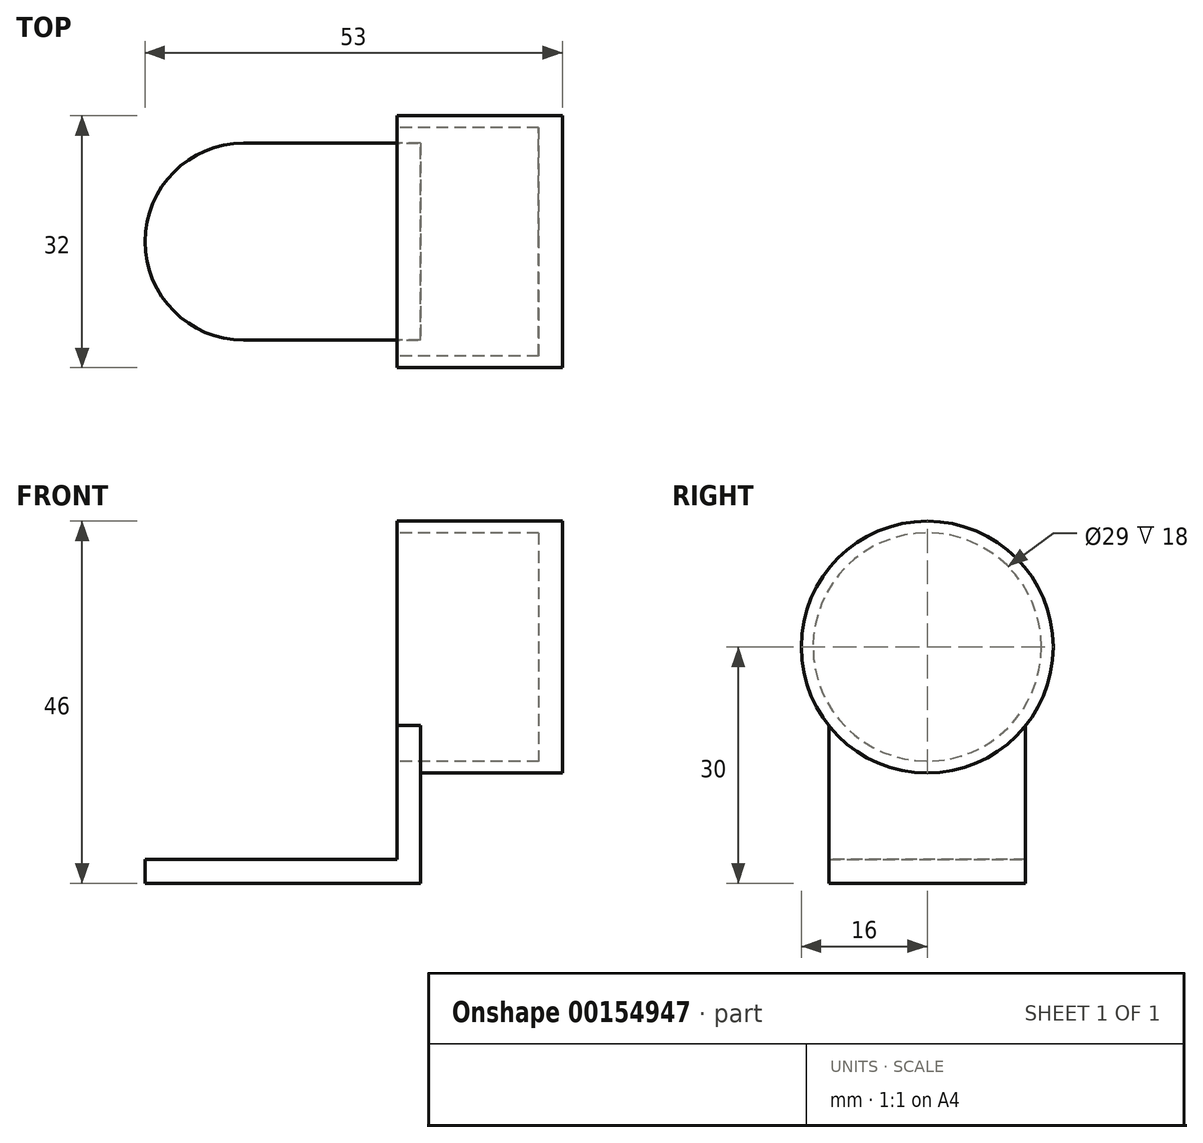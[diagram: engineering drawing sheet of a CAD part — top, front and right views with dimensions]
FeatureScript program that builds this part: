
annotation { "Feature Type Name" : "Feature", "Feature Type Description" : "" }
export const myFeature = defineFeature(function(context is Context, id is Id, definition is map)
    precondition{}
    {
        {
            var Q0;
            Q0=qCreatedBy(makeId("Top.planeOp"),FACE);
            var sketch = newSketch(context, id + "F0", { "sketchPlane" : qUnion([Q0])});
            skLineSegment(sketch, "E0.bottom", {"start": v(-17.5, -12.5) * mm, "end": v(17.5, -12.5) * mm});
            skLineSegment(sketch, "E0.top", {"start": v(-17.5, 12.5) * mm, "end": v(17.5, 12.5) * mm});
            skLineSegment(sketch, "E0.left", {"start": v(-17.5, -12.5) * mm, "end": v(-17.5, 12.5) * mm});
            skLineSegment(sketch, "E0.right", {"start": v(17.5, -12.5) * mm, "end": v(17.5, 12.5) * mm});
            skPoint(sketch, "E0.middle", {"position": v(0, 0) * mm});
            skSolve(sketch);
        }
        {
            var Q0;
            Q0 = qSketchRegion(id + "F0", true);
            extrude(context, id + "F1", {"entities" : qUnion([Q0]), "depth" : 3 * mm});
        }
        {
            var Q0;
            Q0=qCreatedBy(makeId("Top.planeOp"),FACE);
            var sketch = newSketch(context, id + "F2", { "sketchPlane" : qUnion([Q0])});
            skLineSegment(sketch, "E1.bottom", {"start": v(17.5, 12.5) * mm, "end": v(14.5, 12.5) * mm});
            skLineSegment(sketch, "E1.top", {"start": v(17.5, -12.5) * mm, "end": v(14.5, -12.5) * mm});
            skLineSegment(sketch, "E1.left", {"start": v(17.5, 12.5) * mm, "end": v(17.5, -12.5) * mm});
            skLineSegment(sketch, "E1.right", {"start": v(14.5, 12.5) * mm, "end": v(14.5, -12.5) * mm});
            skSolve(sketch);
        }
        {
            var Q0;
            Q0 = qSketchRegion(id + "F2", true);
            extrude(context, id + "F3", {"entities" : qUnion([Q0]), "operationType" : NewBodyOperationType.ADD, "depth" : 40 * mm});
        }
        {
            var Q0;
            Q0=makeQuery(id+"F1.opExtrude","SWEPT_EDGE",EDGE,{"disambiguationData":[OSD([sQuery(id+"F0.wireOp",EDGE,"E0.top"),sQuery(id+"F0.wireOp",EDGE,"E0.left")])]});
            var Q1;
            Q1=makeQuery(id+"F1.opExtrude","SWEPT_EDGE",EDGE,{"disambiguationData":[OSD([sQuery(id+"F0.wireOp",EDGE,"E0.bottom"),sQuery(id+"F0.wireOp",EDGE,"E0.left")])]});
            fillet(context, id + "F4", {"entities" : qUnion([Q0, Q1]), "radius" : 12.5 * mm, "tangentPropagation" : true, "allowEdgeOverflow" : false});
        }
        {
            var Q0;
            Q0=makeQuery(id+"F3.opExtrude","CAP_EDGE",EDGE,{"disambiguationData":[OSD([sQuery(id+"F2.wireOp",EDGE,"E1.bottom")])],"isStart":false});
            var Q1;
            Q1=makeQuery(id+"F3.opExtrude","CAP_EDGE",EDGE,{"disambiguationData":[OSD([sQuery(id+"F2.wireOp",EDGE,"E1.top")])],"isStart":false});
            fillet(context, id + "F5", {"entities" : qUnion([Q0, Q1]), "radius" : 12.5 * mm, "tangentPropagation" : true, "allowEdgeOverflow" : false});
        }
        {
            var Q0;
            Q0=makeQuery(id+"F3.opExtrude","SWEPT_FACE",FACE,{"disambiguationData":[OSD([sQuery(id+"F2.wireOp",EDGE,"E1.right")])]});
            var sketch = newSketch(context, id + "F6", { "sketchPlane" : qUnion([Q0])});
            skCircle(sketch, "E2", {"center": v(0, 30) * mm, "radius": 16 * mm});
            skSolve(sketch);
        }
        {
            var Q0;
            Q0 = qSketchRegion(id + "F6", true);
            extrude(context, id + "F7", {"entities" : qUnion([Q0]), "operationType" : NewBodyOperationType.ADD, "oppositeDirection" : true, "depth" : 21 * mm});
        }
        {
            var Q0;
            Q0=makeQuery(id+"F7.boolean.opBoolean","MERGE",FACE,{"derivedFrom":[makeQuery(id+"F3.opExtrude","SWEPT_FACE",FACE,{"disambiguationData":[OSD([sQuery(id+"F2.wireOp",EDGE,"E1.right")])]}),makeQuery(id+"F7.opExtrude","CAP_FACE",FACE,{"disambiguationData":[OSD([sQuery(id+"F6.wireOp",EDGE,"E2")])],"isStart":true})]});
            var sketch = newSketch(context, id + "F8", { "sketchPlane" : qUnion([Q0])});
            skCircle(sketch, "E3", {"center": v(0, 30) * mm, "radius": 14.5 * mm});
            skSolve(sketch);
        }
        {
            var Q0;
            Q0 = qSketchRegion(id + "F8", true);
            extrude(context, id + "F9", {"entities" : qUnion([Q0]), "operationType" : NewBodyOperationType.REMOVE, "oppositeDirection" : true, "depth" : 18 * mm});
        }
    });
